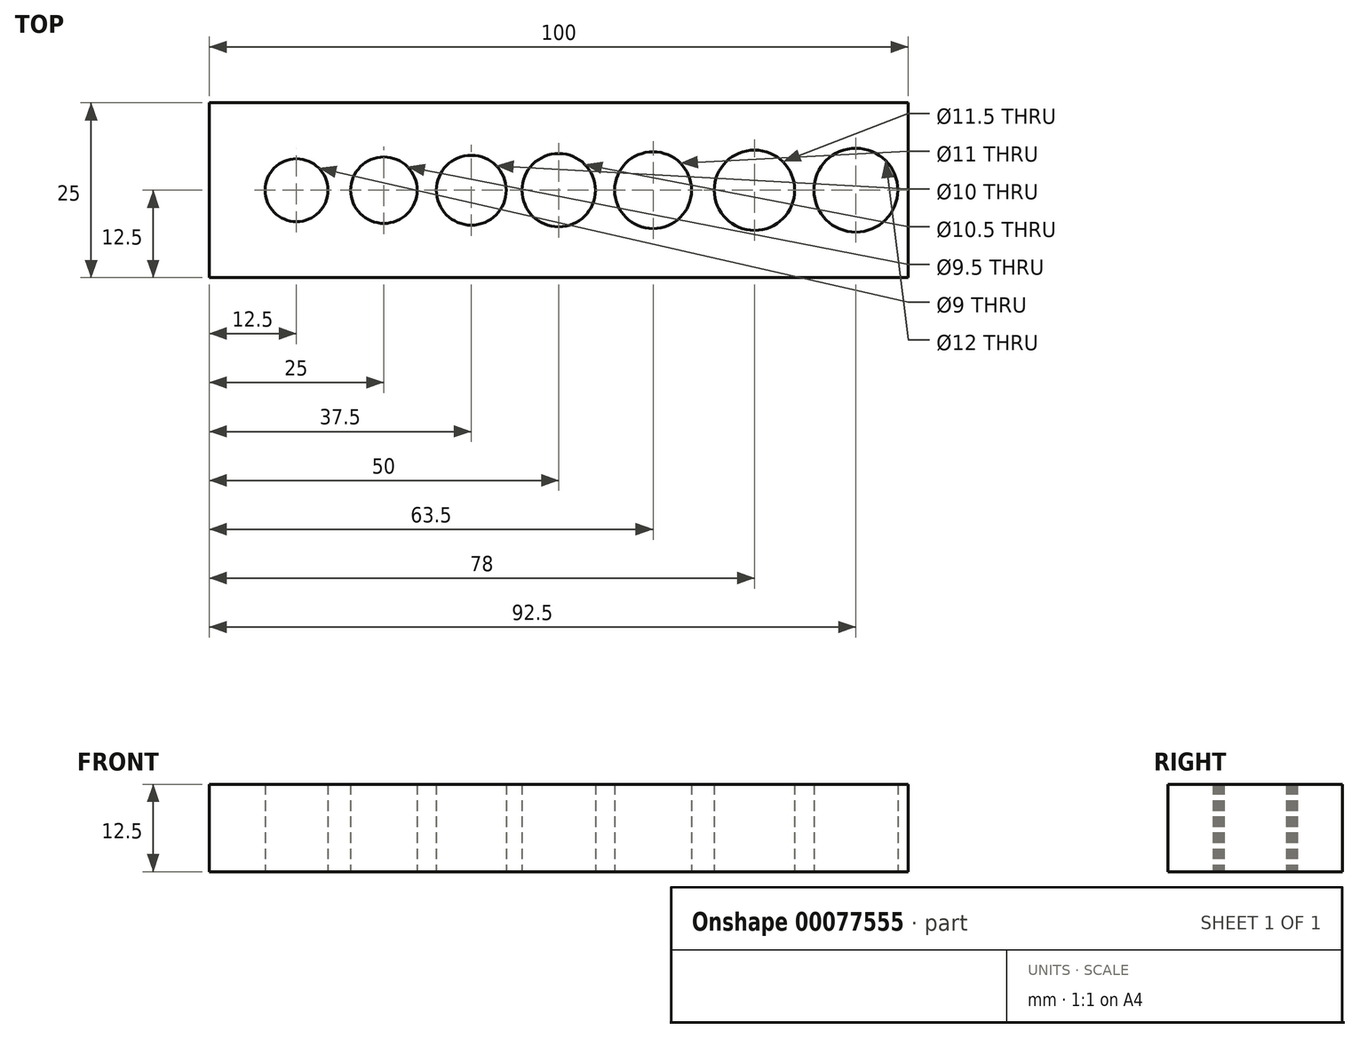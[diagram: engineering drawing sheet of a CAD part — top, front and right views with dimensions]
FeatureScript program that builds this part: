
annotation { "Feature Type Name" : "Feature", "Feature Type Description" : "" }
export const myFeature = defineFeature(function(context is Context, id is Id, definition is map)
    precondition{}
    {
        {
            var Q0;
            Q0=qCreatedBy(makeId("Top.planeOp"),FACE);
            var sketch = newSketch(context, id + "F0", { "sketchPlane" : qUnion([Q0])});
            skLineSegment(sketch, "E0.bottom", {"start": v(0, 0) * mm, "end": v(100, 0) * mm});
            skLineSegment(sketch, "E0.top", {"start": v(0, 25) * mm, "end": v(100, 25) * mm});
            skLineSegment(sketch, "E0.left", {"start": v(0, 0) * mm, "end": v(0, 25) * mm});
            skLineSegment(sketch, "E0.right", {"start": v(100, 0) * mm, "end": v(100, 25) * mm});
            skLineSegment(sketch, "E1", {"start": v(0, 12.5) * mm, "end": v(100, 12.5) * mm, "construction": true});
            skCircle(sketch, "E2", {"center": v(12.5, 12.5) * mm, "radius": 4.5 * mm});
            skCircle(sketch, "E3", {"center": v(25, 12.5) * mm, "radius": 4.75 * mm});
            skCircle(sketch, "E4", {"center": v(50, 12.5) * mm, "radius": 5.25 * mm});
            skCircle(sketch, "E5", {"center": v(37.5, 12.5) * mm, "radius": 5 * mm});
            skCircle(sketch, "E6", {"center": v(63.5, 12.5) * mm, "radius": 5.5 * mm});
            skCircle(sketch, "E7", {"center": v(78, 12.5) * mm, "radius": 5.75 * mm});
            skCircle(sketch, "E8", {"center": v(92.5, 12.5) * mm, "radius": 6 * mm});
            skSolve(sketch);
        }
        {
            var Q0;
            Q0=makeQuery(id+"F0.imprint","IMPRINT",FACE,{"disambiguationData":[TD([[makeQuery(id+"F0.imprint","IMPRINT",EDGE,{"derivedFrom":sQuery(id+"F0.wireOp",EDGE,"E0.bottom")}),1.0]])]});
            extrude(context, id + "F1", {"entities" : qUnion([Q0]), "depth" : 12.5 * mm});
        }
    });
